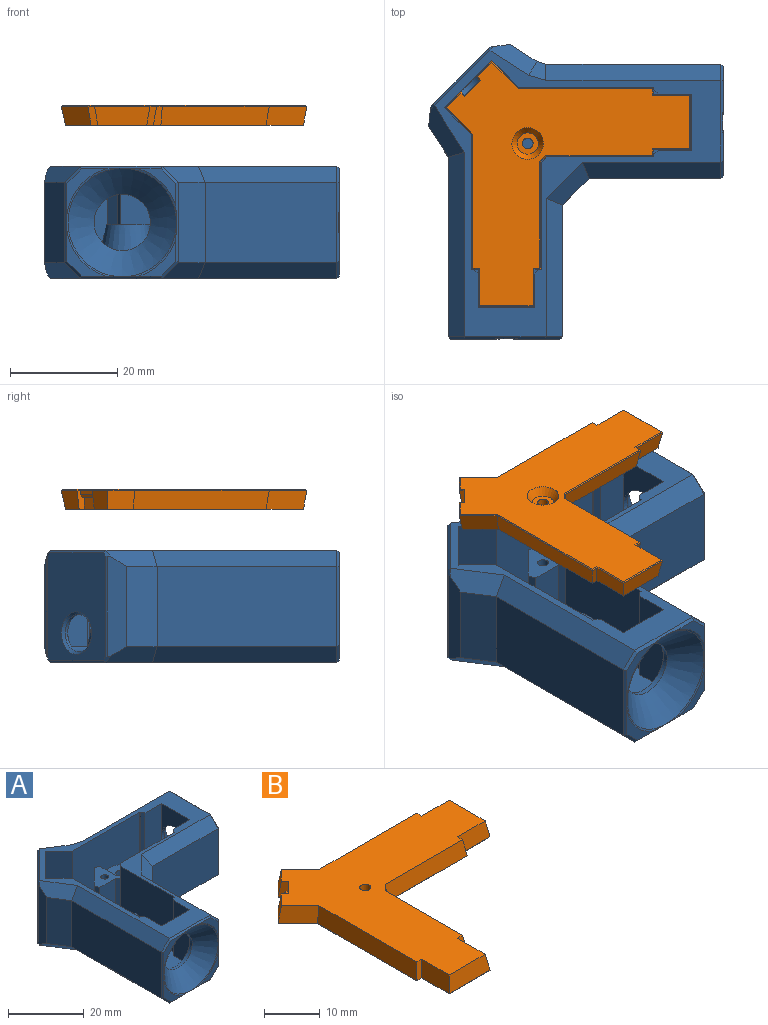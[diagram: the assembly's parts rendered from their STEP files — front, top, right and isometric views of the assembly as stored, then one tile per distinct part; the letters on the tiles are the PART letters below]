
ASSEMBLY  parts=2 mates=1
PART A: 114 faces, bbox 55x55x20.9 mm
  f0: plane 8.48x7.27mm, normal (0,-1,0), area 14.9mm2, adj f105,f107,f108,f110
  f1: plane 6.91x6.91mm, normal (0,-1,0), area 12.2mm2, adj f107,f109,f110,f111
  f2: plane 6.91x6.91mm, normal (0,-1,0), area 12.2mm2, adj f104,f106,f107,f109
  f3: plane 8.48x7.27mm, normal (1,0,0), area 14.9mm2, adj f94,f95,f96,f98
  f4: plane 6.91x6.91mm, normal (1,0,0), area 12.2mm2, adj f96,f98,f99,f101
  f5: plane 6.91x6.91mm, normal (1,0,0), area 12.2mm2, adj f98,f100,f101,f102
  f6: plane 46.03x46.03mm, normal (0,0,1), area 672.2mm2, adj f9,f10,f11,f12,f13,f14,f15,f16
  f7: plane 10.5x10.47mm, normal (0,1,0), area 66.6mm2, adj f10,f35,f36,f43
  f8: plane 10.5x10.47mm, normal (-1,0,0), area 66.6mm2, adj f18,f20,f36,f42
  f9: plane 10.5x7.47mm, normal (0,1,0), area 35.1mm2, adj f6,f10,f35,f43
  f10: plane 17.94x6.17mm, normal (1,0,0), area 110.7mm2, adj f6,f7,f9,f36,f81
  f11: plane 17.94x0.42mm, normal (0,1,0), area 7.6mm2, adj f6,f12,f36,f81
  f12: plane 25.16x17.94mm, normal (1,0,0), area 451.4mm2, adj f6,f11,f13,f36
  f13: plane 17.94x5.03mm, normal (0.71,0.71,0), area 127.6mm2, adj f6,f12,f14,f36
  f14: plane 17.94x8.84mm, normal (0.71,-0.71,0), area 174.5mm2, adj f6,f13,f15,f36,f78
  f15: plane 17.94x5.03mm, normal (-0.71,-0.71,0), area 127.6mm2, adj f6,f14,f16,f36
  f16: plane 25.16x17.94mm, normal (0,-1,0), area 451.4mm2, adj f6,f15,f17,f36
  f17: plane 17.94x0.42mm, normal (-1,0,0), area 7.6mm2, adj f6,f16,f36,f80
  f18: plane 17.94x6.17mm, normal (0,-1,0), area 110.7mm2, adj f6,f8,f19,f36,f80
  f19: plane 10.5x7.47mm, normal (-1,0,0), area 35.1mm2, adj f6,f18,f20,f42
  f20: plane 17.94x6.17mm, normal (0,1,0), area 110.7mm2, adj f6,f8,f19,f36,f79
  f21: plane 17.94x0.42mm, normal (-1,0,0), area 7.6mm2, adj f6,f22,f36,f79
  f22: plane 20x17.94mm, normal (0,1,0), area 358.8mm2, adj f6,f21,f23,f36,f49
  f23: plane 3.94x1mm, normal (-0.71,0.71,0), area 5.6mm2, adj f22,f24,f36,f55
  f24: plane 20x17.94mm, normal (-1,0,0), area 358.8mm2, adj f6,f23,f25,f36,f53
  f25: plane 17.94x0.42mm, normal (0,1,0), area 7.6mm2, adj f6,f24,f36,f82
  f26: plane 14.94x5.01mm, normal (0.54,0.84,0), area 88.7mm2, adj f66,f68,f69,f71
  f27: plane 19.97x10.85mm, normal (-0.71,0.71,0), area 256mm2, adj f85,f86,f87,f88,f89,f90,f91,f92
  f28: plane 14.94x5.75mm, normal (-0.84,-0.54,0), area 101.8mm2, adj f29,f60,f61,f62
  f29: plane 33.52x14.94mm, normal (-1,0,0), area 500.7mm2, adj f28,f59,f63,f105
  f30: plane 8.48x7.27mm, normal (0,-1,0), area 14.9mm2, adj f103,f104,f105,f107
  f31: plane 24.55x14.94mm, normal (1,0,0), area 366.7mm2, adj f44,f57,f72,f109
  f32: plane 24.55x14.94mm, normal (0,-1,0), area 366.7mm2, adj f44,f56,f73,f101
  f33: plane 8.48x7.27mm, normal (1,0,0), area 14.9mm2, adj f95,f97,f98,f100
  f34: plane 32.64x14.94mm, normal (0,1,0), area 487.7mm2, adj f64,f67,f68,f95
  f35: plane 17.94x6.17mm, normal (-1,0,0), area 110.7mm2, adj f6,f7,f9,f36,f82
  f36: plane 53.35x53.35mm, normal (0,0,1), area 417.2mm2, adj f7,f8,f10,f11,f12,f13,f14,f15
  f37: plane 53.35x53.35mm, normal (0,0,-1), area 1331mm2, adj f56,f57,f58,f62,f63,f67,f70,f71
  f38: cylinder r=1.5mm len=7mm, axis (0,0,-1), area 66mm2, adj f39,f75
  f39: plane 8x8mm, normal (0,0,1), area 43.2mm2, adj f38,f113
  f40: cylinder r=1.5mm len=7mm, axis (0,0,-1), area 66mm2, adj f41,f76
  f41: plane 8x8mm, normal (0,0,1), area 43.2mm2, adj f40,f112
  f42: cylinder r=5.25mm len=10.5mm, axis (1,0,0), area 33mm2, adj f8,f19,f45
  f43: cylinder r=5.25mm len=10.5mm, axis (0,-1,0), area 33mm2, adj f7,f9,f46
  f44: plane 14.94x5mm, normal (0.71,-0.71,0), area 105.6mm2, adj f31,f32,f58,f74
  f45: cone r=5.25mm half-angle=45deg, axis (1,0,0), area 331.5mm2, adj f42,f98
  f46: cone r=5.25mm half-angle=45deg, axis (0,-1,0), area 331.5mm2, adj f43,f107
  f47: cylinder r=3.5mm len=8.14mm, axis (-0.71,0.71,0), area 35.9mm2, adj f6,f48,f78,f93
  f48: plane 3.46x3.46mm, normal (-0.71,0.71,0), area 3.4mm2, adj f6,f47
  f49: plane 14x1mm, normal (0.71,0.71,0), area 19.8mm2, adj f6,f22,f50,f55
  f50: plane 14x5.84mm, normal (1,0,0), area 81.7mm2, adj f6,f49,f55,f83
  f51: plane 14x6.01mm, normal (-0.71,0.71,0), area 119mm2, adj f6,f55,f83,f84
  f52: plane 14x5.84mm, normal (0,-1,0), area 81.7mm2, adj f6,f53,f55,f84
  f53: plane 14x1mm, normal (-0.71,-0.71,0), area 19.8mm2, adj f6,f24,f52,f55
  f54: cylinder r=1mm len=14mm, axis (0,0,-1), area 88mm2, adj f55,f77
  f55: plane 8.42x8.42mm, normal (0,0,1), area 34.6mm2, adj f23,f49,f50,f51,f52,f53,f54,f83
  f56: plane 25.79x3mm, normal (0,-0.71,-0.71), area 106.8mm2, adj f32,f37,f58,f99
  f57: plane 25.79x3mm, normal (0.71,0,-0.71), area 106.8mm2, adj f31,f37,f58,f106
  f58: plane 8x8mm, normal (0.5,-0.5,-0.71), area 35.3mm2, adj f37,f44,f56,f57
  f59: plane 34.39x3mm, normal (-0.71,0,0.71), area 144.1mm2, adj f29,f36,f60,f108
  f60: plane 9.54x6.66mm, normal (-0.6,-0.38,0.71), area 37.9mm2, adj f28,f36,f59,f61,f88,f90
  f61: plane 18.82x3.56mm, normal (-0.99,0.11,0), area 61.4mm2, adj f28,f60,f62,f85,f86,f88
  f62: plane 9.54x6.66mm, normal (-0.6,-0.38,-0.71), area 37.9mm2, adj f28,f37,f61,f63,f85,f87
  f63: plane 34.39x3mm, normal (-0.71,0,-0.71), area 144.1mm2, adj f29,f37,f62,f103
  f64: plane 32.64x3mm, normal (0,0.71,0.71), area 138.5mm2, adj f34,f36,f65,f97
  f65: plane 3.47x3.22mm, normal (0.2,0.69,0.69), area 10.5mm2, adj f36,f64,f66,f68
  f66: plane 8.81x5.72mm, normal (0.38,0.6,0.71), area 32.3mm2, adj f26,f36,f65,f69,f90,f92
  f67: plane 32.64x3mm, normal (0,0.71,-0.71), area 138.5mm2, adj f34,f37,f70,f94
  f68: plane 14.94x1.61mm, normal (0.28,0.96,0), area 25.1mm2, adj f26,f34,f65,f70
  f69: plane 18.82x3.56mm, normal (-0.11,0.99,0), area 61.4mm2, adj f26,f66,f71,f89,f91,f92
  f70: plane 3.47x3.22mm, normal (0.2,0.69,-0.69), area 10.5mm2, adj f37,f67,f68,f71
  f71: plane 8.81x5.72mm, normal (0.38,0.6,-0.71), area 32.3mm2, adj f26,f37,f69,f70,f87,f89
  f72: plane 25.79x3mm, normal (0.71,0,0.71), area 106.8mm2, adj f31,f36,f74,f111
  f73: plane 25.79x3mm, normal (0,-0.71,0.71), area 106.8mm2, adj f32,f36,f74,f102
  f74: plane 8x8mm, normal (0.5,-0.5,0.71), area 35.3mm2, adj f36,f44,f72,f73
  f75: plane 3x3mm, normal (0,0,1), area 7.1mm2, adj f38
  f76: plane 3x3mm, normal (0,0,1), area 7.1mm2, adj f40
  f77: plane 2x2mm, normal (0,0,1), area 3.1mm2, adj f54
  f78: cone r=4.33mm half-angle=45deg, axis (0.71,-0.71,0), area 20.8mm2, adj f6,f14,f47
  f79: plane 17.94x0.83mm, normal (-0.71,0.71,0), area 21mm2, adj f6,f20,f21,f36
  f80: plane 17.94x0.83mm, normal (-0.71,-0.71,0), area 21mm2, adj f6,f17,f18,f36
  f81: plane 17.94x0.83mm, normal (0.71,0.71,0), area 21mm2, adj f6,f10,f11,f36
  f82: plane 17.94x0.83mm, normal (-0.71,0.71,0), area 21mm2, adj f6,f25,f35,f36
  f83: plane 14x1.41mm, normal (0.38,0.92,0), area 21.4mm2, adj f6,f50,f51,f55
  f84: plane 14x1.41mm, normal (-0.92,-0.38,0), area 21.4mm2, adj f6,f51,f52,f55
  f85: plane 1.19x1.11mm, normal (-0.86,0.22,-0.47), area 0.8mm2, adj f27,f61,f62,f86,f87
  f86: plane 18.81x0.29mm, normal (-0.9,0.43,0), area 6mm2, adj f27,f61,f85,f88
  f87: plane 10.5x10.5mm, normal (-0.5,0.5,-0.71), area 9.9mm2, adj f27,f37,f62,f71,f85,f89
  f88: plane 1.19x1.11mm, normal (-0.86,0.22,0.47), area 0.8mm2, adj f27,f60,f61,f86,f90
  f89: plane 1.19x1.11mm, normal (-0.22,0.86,-0.47), area 0.8mm2, adj f27,f69,f71,f87,f91
  f90: plane 10.5x10.5mm, normal (-0.5,0.5,0.71), area 9.9mm2, adj f27,f36,f60,f66,f88,f92
  f91: plane 18.81x0.29mm, normal (-0.43,0.9,0), area 6mm2, adj f27,f69,f89,f92
  f92: plane 1.19x1.11mm, normal (-0.22,0.86,0.47), area 0.8mm2, adj f27,f66,f69,f90,f91
  f93: cone r=3.5mm half-angle=45deg, axis (-0.71,0.71,0), area 16.1mm2, adj f27,f47
  f94: plane 3.2x3.2mm, normal (0.71,0.5,-0.5), area 2.8mm2, adj f3,f67,f95,f96
  f95: plane 14.94x0.48mm, normal (0.71,0.71,0), area 10mm2, adj f3,f33,f34,f94,f97,f98
  f96: plane 15.29x0.48mm, normal (0.71,0,-0.71), area 9.5mm2, adj f3,f4,f37,f94,f98,f99
  f97: plane 3.2x3.2mm, normal (0.71,0.5,0.5), area 2.8mm2, adj f33,f64,f95,f100
  f98: cone r=10.45mm half-angle=67.5deg, axis (1,0,0), area 19.3mm2, adj f3,f4,f5,f33,f45,f95,f96,f100
  f99: plane 3.2x3.2mm, normal (0.71,-0.5,-0.5), area 2.8mm2, adj f4,f56,f96,f101
  f100: plane 15.29x0.48mm, normal (0.71,0,0.71), area 9.5mm2, adj f5,f33,f36,f97,f98,f102
  f101: plane 14.94x0.48mm, normal (0.71,-0.71,0), area 9.3mm2, adj f4,f5,f32,f98,f99,f102
  f102: plane 3.2x3.2mm, normal (0.71,-0.5,0.5), area 2.8mm2, adj f5,f73,f100,f101
  f103: plane 3.2x3.2mm, normal (-0.5,-0.71,-0.5), area 2.8mm2, adj f30,f63,f104,f105
  f104: plane 15.29x0.48mm, normal (0,-0.71,-0.71), area 9.5mm2, adj f2,f30,f37,f103,f106,f107
  f105: plane 14.94x0.48mm, normal (-0.71,-0.71,0), area 10mm2, adj f0,f29,f30,f103,f107,f108
  f106: plane 3.2x3.2mm, normal (0.5,-0.71,-0.5), area 2.8mm2, adj f2,f57,f104,f109
  f107: cone r=10.45mm half-angle=67.5deg, axis (0,-1,0), area 19.3mm2, adj f0,f1,f2,f30,f46,f104,f105,f109
  f108: plane 3.2x3.2mm, normal (-0.5,-0.71,0.5), area 2.8mm2, adj f0,f59,f105,f110
  f109: plane 14.94x0.48mm, normal (0.71,-0.71,0), area 9.3mm2, adj f1,f2,f31,f106,f107,f111
  f110: plane 15.29x0.48mm, normal (0,-0.71,0.71), area 9.5mm2, adj f0,f1,f36,f107,f108,f111
  f111: plane 3.2x3.2mm, normal (0.5,-0.71,0.5), area 2.8mm2, adj f1,f72,f109,f110
  f112: cone r=4mm half-angle=12.1deg, axis (0,0,-1), area 213.7mm2, adj f6,f41
  f113: cone r=4mm half-angle=12.1deg, axis (0,0,-1), area 213.7mm2, adj f6,f39
PART B: 53 faces, bbox 45.8x45.8x3.7 mm
  f0: plane 3.53x1.35mm, normal (-0.71,-0.71,0), area 4.5mm2, adj f1,f4,f24,f27,f28,f29,f46,f48
  f1: plane 2.83x2.83mm, normal (-0.71,0.71,0), area 8.8mm2, adj f0,f2,f4,f28
  f2: plane 3.53x1.35mm, normal (0.71,0.71,0), area 4.5mm2, adj f1,f4,f8,f27,f28,f29,f51,f52
  f3: cylinder r=1mm len=2.2mm, axis (0,0,-1), area 13.8mm2, adj f4,f6
  f4: plane 44.34x44.34mm, normal (0,0,1), area 785.4mm2, adj f0,f1,f2,f3,f8,f9,f10,f11
  f5: plane 45.42x45.42mm, normal (0,0,-1), area 837.8mm2, adj f7,f31,f32,f33,f34,f35,f36,f37
  f6: plane 3.98x3.98mm, normal (0,0,-1), area 9.3mm2, adj f3,f30
  f7: cone r=2.95mm half-angle=9.9deg, axis (0,0,-1), area 0.4mm2, adj f5,f30
  f8: plane 3.5x3.38mm, normal (-0.7,0.7,0.17), area 13.7mm2, adj f2,f4,f9,f51
  f9: plane 5.61x5mm, normal (-0.7,-0.7,0.17), area 24.5mm2, adj f4,f8,f10,f49
  f10: plane 25.36x3.5mm, normal (-0.99,0,0.17), area 88.7mm2, adj f4,f9,f11,f47
  f11: plane 3.5x1.86mm, normal (0,-0.99,0.17), area 4.4mm2, adj f4,f10,f12,f45
  f12: plane 7.61x3.5mm, normal (-0.99,0,0.17), area 24.9mm2, adj f4,f11,f13,f43
  f13: plane 10.33x3.5mm, normal (0,-0.99,0.17), area 34.5mm2, adj f4,f12,f14,f41
  f14: plane 7.61x3.5mm, normal (0.99,0,0.17), area 24.9mm2, adj f4,f13,f15,f39
  f15: plane 3.5x1.86mm, normal (0,-0.99,0.17), area 4.4mm2, adj f4,f14,f16,f37
  f16: plane 20.2x3.5mm, normal (0.99,0,0.17), area 70.3mm2, adj f4,f15,f17,f35
  f17: plane 3.5x1.66mm, normal (0.7,-0.7,0.17), area 6.2mm2, adj f4,f16,f18,f33
  f18: plane 20.2x3.5mm, normal (0,-0.99,0.17), area 70.3mm2, adj f4,f17,f19,f31
  f19: plane 3.5x1.86mm, normal (0.99,0,0.17), area 4.4mm2, adj f4,f18,f20,f32
  f20: plane 7.61x3.5mm, normal (0,-0.99,0.17), area 24.9mm2, adj f4,f19,f21,f34
  f21: plane 10.33x3.5mm, normal (0.99,0,0.17), area 34.5mm2, adj f4,f20,f22,f36
  f22: plane 7.61x3.5mm, normal (0,0.99,0.17), area 24.9mm2, adj f4,f21,f23,f38
  f23: plane 3.5x1.86mm, normal (0.99,0,0.17), area 4.4mm2, adj f4,f22,f25,f40
  f24: plane 3.5x3.38mm, normal (-0.7,0.7,0.17), area 13.7mm2, adj f0,f4,f26,f46
  f25: plane 25.36x3.5mm, normal (0,0.99,0.17), area 88.7mm2, adj f4,f23,f26,f42
  f26: plane 5.61x5mm, normal (0.7,0.7,0.17), area 24.5mm2, adj f4,f24,f25,f44
  f27: plane 2.83x2.83mm, normal (-0.71,0.71,0), area 3.3mm2, adj f0,f2,f29,f50
  f28: plane 3.18x3.18mm, normal (0,0,1), area 2mm2, adj f0,f1,f2,f29
  f29: plane 3.18x3.18mm, normal (-0.5,0.5,0.71), area 2.8mm2, adj f0,f2,f27,f28
  f30: cone r=1.99mm half-angle=33deg, axis (0,0,-1), area 27.3mm2, adj f6,f7
  f31: plane 20.02x0.2mm, normal (0,-0.77,-0.64), area 5.1mm2, adj f5,f18,f32,f33
  f32: plane 1.42x0.2mm, normal (0.77,0,-0.64), area 0.3mm2, adj f5,f19,f31,f34
  f33: plane 1.22x1.22mm, normal (0.54,-0.54,-0.64), area 0.4mm2, adj f5,f17,f31,f35
  f34: plane 7.17x0.2mm, normal (0,-0.77,-0.64), area 1.8mm2, adj f5,f20,f32,f36
  f35: plane 20.02x0.2mm, normal (0.77,0,-0.64), area 5.1mm2, adj f5,f16,f33,f37
  f36: plane 10.33x0.2mm, normal (0.77,0,-0.64), area 2.6mm2, adj f5,f21,f34,f38
  f37: plane 1.42x0.2mm, normal (0,-0.77,-0.64), area 0.3mm2, adj f5,f15,f35,f39
  f38: plane 7.17x0.2mm, normal (0,0.77,-0.64), area 1.8mm2, adj f5,f22,f36,f40
  f39: plane 7.17x0.2mm, normal (0.77,0,-0.64), area 1.8mm2, adj f5,f14,f37,f41
  f40: plane 1.42x0.2mm, normal (0.77,0,-0.64), area 0.3mm2, adj f5,f23,f38,f42
  f41: plane 10.33x0.2mm, normal (0,-0.77,-0.64), area 2.6mm2, adj f5,f13,f39,f43
  f42: plane 25.18x0.2mm, normal (0,0.77,-0.64), area 6.4mm2, adj f5,f25,f40,f44
  f43: plane 7.17x0.2mm, normal (-0.77,0,-0.64), area 1.8mm2, adj f5,f12,f41,f45
  f44: plane 5.16x5mm, normal (0.54,0.54,-0.64), area 1.8mm2, adj f5,f26,f42,f46
  f45: plane 1.42x0.2mm, normal (0,-0.77,-0.64), area 0.3mm2, adj f5,f11,f43,f47
  f46: plane 2.96x2.94mm, normal (-0.54,0.54,-0.64), area 1mm2, adj f0,f5,f24,f44,f48
  f47: plane 25.18x0.2mm, normal (-0.77,0,-0.64), area 6.4mm2, adj f5,f10,f45,f49
  f48: plane 0.87x0.65mm, normal (-0.5,-0.5,-0.71), area 0.2mm2, adj f0,f5,f46,f50
  f49: plane 5.16x5mm, normal (-0.54,-0.54,-0.64), area 1.8mm2, adj f5,f9,f47,f51
  f50: plane 3.07x3.07mm, normal (-0.5,0.5,-0.71), area 1mm2, adj f5,f27,f48,f52
  f51: plane 2.96x2.94mm, normal (-0.54,0.54,-0.64), area 1mm2, adj f2,f5,f8,f49,f52
  f52: plane 0.87x0.65mm, normal (0.5,0.5,-0.71), area 0.2mm2, adj f2,f5,f50,f51
PLACE A t=(3.19,8.9,-13.47)mm
PLACE B rot(axis=(0.71,-0.71,0),180deg) t=(2.55,11.4,18.84)mm
MATE slider B.f3 <-> A.f54  axis (0,0,-1) through (0.69,11.4,15.14)mm
